# Revit family: BAXI_BC_ACS_SPLIT_150_(UI_Acumulador)
name_source: partatom
category: Equipos mecánicos
units: mm (PartAtom-declared; Revit-internal decimal feet)

## family parameters
Compartido = No
Corte con vacíos al cargar = No
Cota de conector redondo = Diámetro de uso
Número OmniClass = 23.65.35.11.11
Punto de cálculo de habitación = No
Se basa en plano de trabajo = No
Siempre vertical = Sí
Tipo de pieza = Normal
Título OmniClass = Storage Water Heaters

## types (1)
- BC ACS SPLIT 150 (UI)
    Altura = 1273 mm  [stored 4.17651 ft]
    Anchura = 566 mm  [stored 1.85696 ft]
    BIMETRICAL = http://www.bimetrical.com
    BIMETRICAL Category = Tank
    Capacidad_Frig_Gas = 0.0 L/s
    Capacidad_Frig_Líquido = 0.0 L/s
    Caudal_ACS = 0.0 L/s
    Caudal_AFS = 0.0 L/s
    Clase Eficiencia Energética ACS/Perfil demanda = A+/L
    Conjunto compatible = SPLIT 150-200-300 (UE)
    Consumo eléctrico medio = 900 W
    Creado por = BIMETRICAL
    D_Pulgadas_ACS = 3/4''
    D_Pulgadas_AFS = 3/4''
    D_Pulgadas_Frig_Gas = 3/8''
    D_Pulgadas_Frig_Líquido = 1/4''
    Descripción = Alta eficiencia: las bombas de calor BC ACS 150/200/300 Split tienen un rendimiento muy elevado, que permite conseguir ahorros muy importantes respecto a otros equipos de generación de agua caliente sanitaria.
Confort: la bomba de calor puede calentar el agua hasta 65ºC. Además, el equipo incluye una resistencia eléctrica de 2,4 kW para los modelos 200/300 y de 1,6 kW para el modelo de 150 que puede ser activada para calentar de manera más rápida el agua del acumulador, permitiendo alcanzar una temperatura de hasta 70ºC para el tratamiento antilegionela.
Robustez, durabilidad y fiabilidad: el acumulador está fabricado en acero esmaltado, e incorpora ánodo de magnesio para evitar la corrosión de éste.
Optimización del espacio: los dos módulos separados permiten ubicar la unidad interior en lugares cerrados y reducidos, aprovechando el espacio habitable, y evitando el ruido producido por el compresor porque se encuentra integrado en la unidad exterior.
    Dext_Cu_Frig_ACS = 19.05 mm
    Dext_Cu_Frig_AFS = 19.05 mm
    Dext_Cu_Frig_Gas = 9.52 mm
    Dext_Cu_Frig_Líquido = 6.35 mm
    Diferencia máx. altura entre módulos = 10 m
    Dn_Métrico_ACS = 20.00 mm
    Dn_Métrico_AFS = 20.00 mm
    Dn_Métrico_Frig_Gas = 10.00 mm
    Dn_Métrico_Frig_Líquido = 6.00 mm
    Fabricante = BAXI
    Fecha de Revisión = 09/2018
    Frecuencia = 50 Hz
    IfcExportAs = IfcTankType
    IfcExportType = STORAGE
    Instalación = Mural
    Longitud = 548 mm  [stored 1.7979 ft]
    Longitud conexión frigorífica (mín/máx) = 2 a 20 m
    Material principal = BAXI_Acero esmaltado
    Material secundario = BAXI_Gris
    Material y Acabados = Acero esmaltado
    Modelo = BC ACS 150 SPLIT
    Peso en vacío = 60.50 kg
    Potencia acústica (dB(A)) = 15
    Potencia eléctrica absorbida (UE) = 900 W
    Potencia resistencia eléctrica apoyo = 1600 W
    Producto = Bombas de calor de ACS
    Tensión alimentación = 230 V
    Tipo de unidad = Unidad Interior
    URL = https://www.baxi.es
    URL PRODUCTO = https://www.baxi.es
    Versión Familia = 1.0
    Versión Revit = Revit 2016 - Español
    Volumen Acumulador = 150 L

note: [stored X ft] marks values corroborated as IEEE doubles in the binary element streams (Revit-internal decimal feet)
